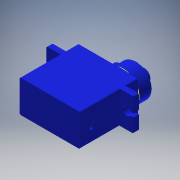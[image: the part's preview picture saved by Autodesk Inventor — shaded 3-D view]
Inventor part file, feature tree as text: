
AUTODESK INVENTOR PART (.ipt)
format: ipt  version: 2016 (Build 200138000, 138)  size: 239,616 bytes
history: native  units: in
note: dims shown in document units (in); Inventor stores cm internally (conversion verified against a paired STEP export)
features: sketch x6, other x4
ambient origin geometry x8: Origin, YZ Plane, XZ Plane, XY Plane, X Axis, Y Axis, Z Axis, Center Point
bodies: Solid1 (feature_tree)
feature tree (10):
  other  "Servo Motor SG90_correct_size.ipt"
  other  "솔리드1::Servo Motor SG90_correct_size.ipt"
  other  "TaggingFeature1"
  sketch  "스케치1"
  sketch  "스케치2"
  sketch  "스케치3"
  sketch  "스케치4"
  sketch  "스케치6"
  sketch  "Sketch7"  dims[d0=0.3937in]
  other  "작업 평면1"
